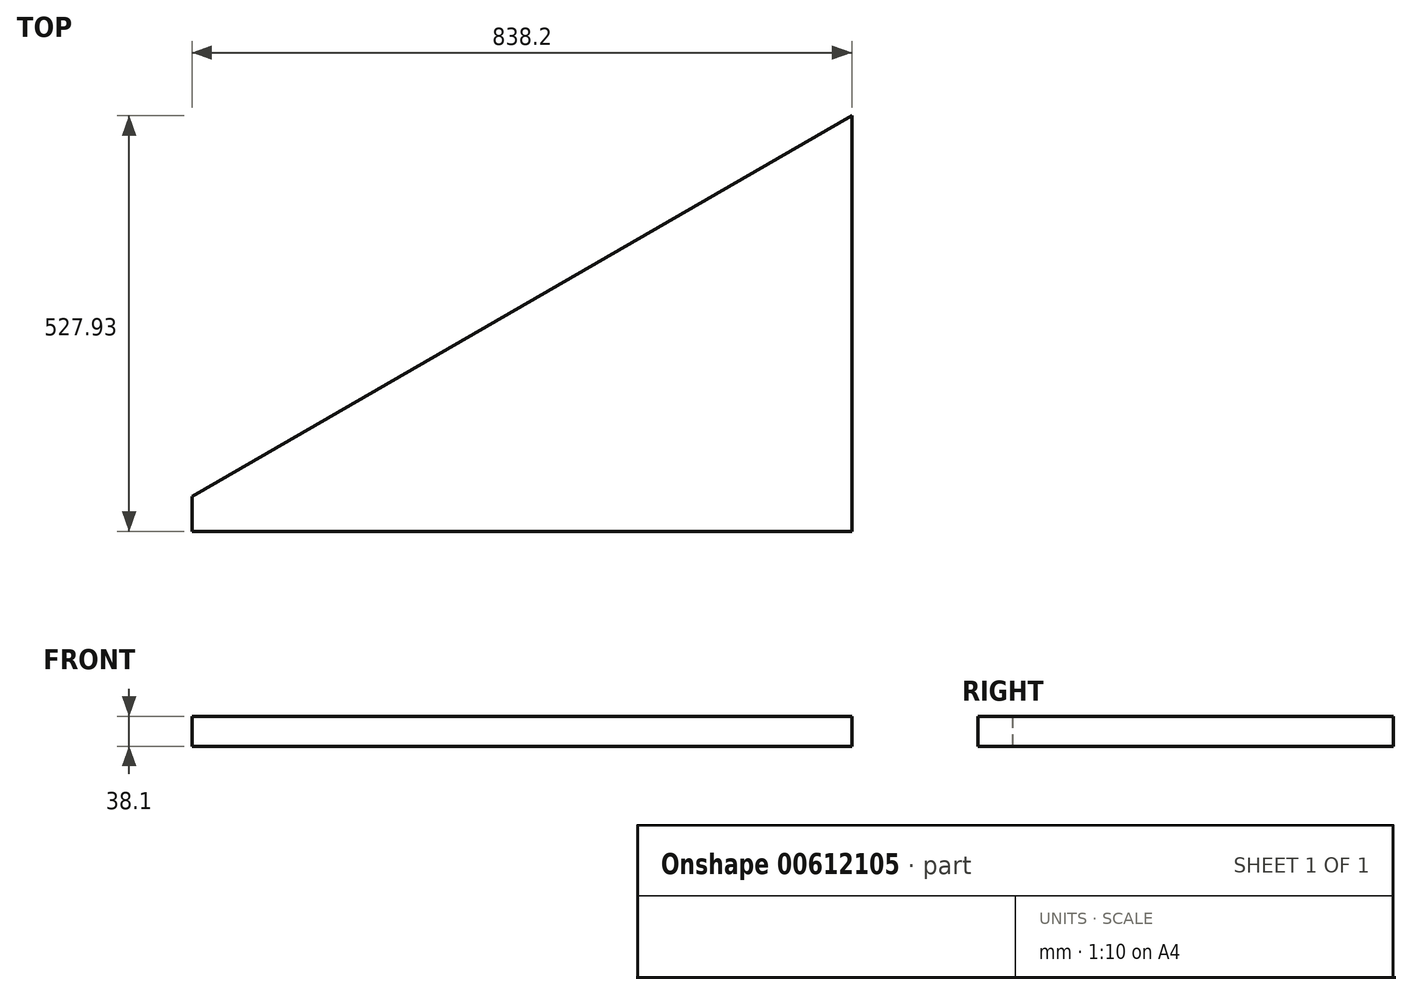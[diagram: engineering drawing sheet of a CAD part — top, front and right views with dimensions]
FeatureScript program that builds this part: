
annotation { "Feature Type Name" : "Feature", "Feature Type Description" : "" }
export const myFeature = defineFeature(function(context is Context, id is Id, definition is map)
    precondition{}
    {
        {
            var Q0;
            Q0=qCreatedBy(makeId("Top.planeOp"),FACE);
            var sketch = newSketch(context, id + "F0", { "sketchPlane" : qUnion([Q0])});
            skLineSegment(sketch, "E0.bottom", {"start": v(76.2, 69.85) * mm, "end": v(-76.2, 69.85) * mm});
            skLineSegment(sketch, "E0.top", {"start": v(76.2, -69.85) * mm, "end": v(-76.2, -69.85) * mm});
            skLineSegment(sketch, "E0.left", {"start": v(76.2, 69.85) * mm, "end": v(76.2, -69.85) * mm});
            skLineSegment(sketch, "E0.right", {"start": v(-76.2, 69.85) * mm, "end": v(-76.2, -69.85) * mm});
            skPoint(sketch, "E0.middle", {"position": v(0, 0) * mm});
            skLineSegment(sketch, "E1.bottom", {"start": v(914.4, 914.4) * mm, "end": v(-914.4, 914.4) * mm});
            skLineSegment(sketch, "E1.top", {"start": v(914.4, -914.4) * mm, "end": v(-914.4, -914.4) * mm});
            skLineSegment(sketch, "E1.left", {"start": v(914.4, 914.4) * mm, "end": v(914.4, -914.4) * mm});
            skLineSegment(sketch, "E1.right", {"start": v(-914.4, 914.4) * mm, "end": v(-914.4, -914.4) * mm});
            skCircle(sketch, "E2", {"center": v(0, 0) * mm, "radius": 1293.16 * mm});
            skLineSegment(sketch, "E3", {"start": v(0, 0) * mm, "end": v(1293.16, 0) * mm});
            skLineSegment(sketch, "E4.1.0", {"start": v(0, 0) * mm, "end": v(1119.9, 646.58) * mm});
            skLineSegment(sketch, "E4.2.0", {"start": v(0, 0) * mm, "end": v(646.58, 1119.9) * mm});
            skLineSegment(sketch, "E4.3.0", {"start": v(0, 0) * mm, "end": v(0, 1293.16) * mm});
            skLineSegment(sketch, "E4.4.0", {"start": v(0, 0) * mm, "end": v(-646.58, 1119.9) * mm});
            skLineSegment(sketch, "E4.5.0", {"start": v(0, 0) * mm, "end": v(-1119.9, 646.58) * mm});
            skLineSegment(sketch, "E4.6.0", {"start": v(0, 0) * mm, "end": v(-1293.16, 0) * mm});
            skLineSegment(sketch, "E4.7.0", {"start": v(0, 0) * mm, "end": v(-1119.9, -646.58) * mm});
            skLineSegment(sketch, "E4.8.0", {"start": v(0, 0) * mm, "end": v(-646.58, -1119.9) * mm});
            skLineSegment(sketch, "E4.9.0", {"start": v(0, 0) * mm, "end": v(0, -1293.16) * mm});
            skLineSegment(sketch, "E4.10.0", {"start": v(0, 0) * mm, "end": v(646.58, -1119.9) * mm});
            skLineSegment(sketch, "E4.11.0", {"start": v(0, 0) * mm, "end": v(1119.9, -646.58) * mm});
            skSolve(sketch);
        }
        {
            var Q0;
            {var subQ0=sQuery(id+"F0.wireOp",EDGE,"E4.1.0");var subQ1=sQuery(id+"F0.wireOp",EDGE,"E0.left");var subQ2=makeQuery(id+"F0.imprint","INTERSECT",VERTEX,{"derivedFrom":[subQ1,subQ0]});Q0=makeQuery(id+"F0.imprint","IMPRINT",FACE,{"disambiguationData":[TD([[makeQuery(id+"F0.imprint","IMPRINT",EDGE,{"disambiguationData":[TD([[subQ2,-1.0]])],"derivedFrom":subQ1}),1.0]])]});}
            extrude(context, id + "F1", {"entities" : qUnion([Q0]), "depth" : 38.1 * mm, "offsetDistance" : 25.4 * mm});
        }
    });
